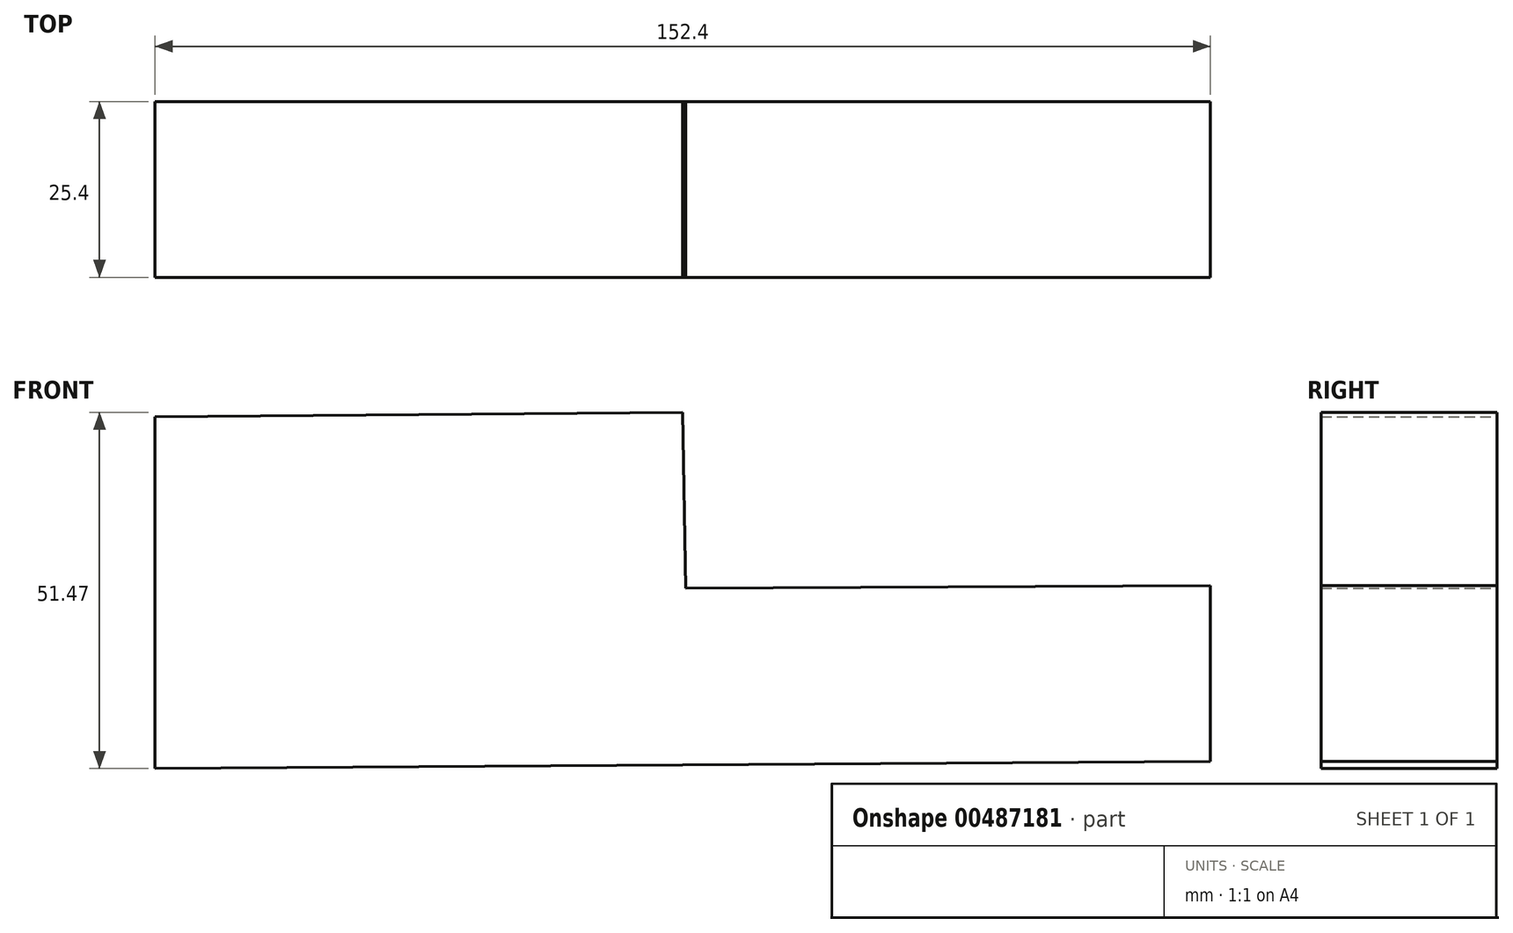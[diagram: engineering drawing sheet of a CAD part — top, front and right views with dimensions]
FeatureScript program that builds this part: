
annotation { "Feature Type Name" : "Feature", "Feature Type Description" : "" }
export const myFeature = defineFeature(function(context is Context, id is Id, definition is map)
    precondition{}
    {
        {
            var Q0;
            Q0=qCreatedBy(makeId("Front.planeOp"),FACE);
            var sketch = newSketch(context, id + "F0", { "sketchPlane" : qUnion([Q0])});
            skLineSegment(sketch, "E0", {"start": v(66.78, 5.8) * mm, "end": v(66.78, 31.2) * mm});
            skLineSegment(sketch, "E1", {"start": v(66.78, 31.2) * mm, "end": v(-9.02, 30.83) * mm});
            skLineSegment(sketch, "E2", {"start": v(-9.02, 30.83) * mm, "end": v(-9.42, 56.23) * mm});
            skLineSegment(sketch, "E3", {"start": v(-9.42, 56.23) * mm, "end": v(-85.62, 55.56) * mm});
            skLineSegment(sketch, "E4", {"start": v(-85.62, 55.56) * mm, "end": v(-85.62, 4.76) * mm});
            skLineSegment(sketch, "E5", {"start": v(-85.62, 4.76) * mm, "end": v(66.78, 5.8) * mm});
            skSolve(sketch);
        }
        {
            var Q0;
            Q0 = qSketchRegion(id + "F0", true);
            extrude(context, id + "F1", {"entities" : qUnion([Q0]), "depth" : 25.4 * mm});
        }
    });
